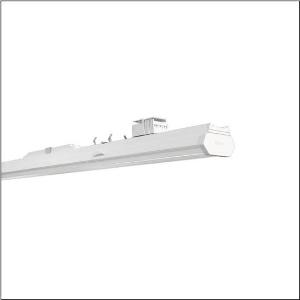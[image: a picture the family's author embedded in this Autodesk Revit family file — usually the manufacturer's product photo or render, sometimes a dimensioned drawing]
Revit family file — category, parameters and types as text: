
# Revit family: licross_r__11_protected_ho_51td13mn4gxs_7737
name_source: partatom
category: Lighting Fixtures
units: mm (PartAtom-declared; Revit-internal decimal feet)

## family parameters
Cut with Voids When Loaded = No
Host = Face
Light Source = No
Part Type = Normal
Room Calculation Point = No
Round Connector Dimension = Use Diameter
Shared = No

## types (1)
- --- (1 x LED, 16110 lm, 87.4 W, 4000K)
    Apparent Load = 87 VA
    CIE Flux Codes = 89 96 99 100 99
    Color Rendering = 80
    Color Temperature = 4000K
    Default Elevation = 1800 mm
    Description = Licross® 11 Protected HO, luminaire insert, of sheet steel, galvanised, coil coated, white, length: 1.500mm, width: 90mm, height: 101mm, LED rated luminous flux: 16.110lm, light colour: 840, control gear: ON/OFF Multilumen, with plug, 3-pole, with phase selection, mains connection: 220..240V, AC, 50/60Hz, rated input power: 87W, halogen-free wiring, primary light control with lens, of plastic, primary optical cover: cover, of PMMA, light emission: direct distribution, primary light characteristic: symmetric, protection rating (complete): IP54, insulation class (complete): insulation class I (protective earthing), certification: CE, ENEC, VDE, UKCA, protection symbol: D if used in an environment with non-conductive dust loads with corresponding accessories, impact resistance: IK06, permissible ambient temperature for indoor applications: -35..+35°C, corresponds to IFS (International Featured Standards) requirements for safety and quality in the food industry, reducing of maximum allowable ambient temperature of 5°C with ceiling mounting, LABS conformity tested according to VDMA 24364:2018-05, packaging unit: 1 piece
    Height = 92 mm
    Lamp = 1 x LED
    Lamp Light Flux = 16110 lm
    Lamp Power = 87.4 W
    Lamp count = 1
    Length = 1500 mm
    Luminous efficacy = 184 lm/W
    Manufacturer = Siteco
    ModVariant = No
    Model = 51TD13MN4GXS
    Mounting Place = Ceiling
    Mounting Type = Pendant
    Number of Poles = 1
    OnlyDefault = Yes
    Power Factor = 1
    Product Name = Licross® 11 Protected HO
    Product group = luminaire insert
    ProductGroupID = 901
    Protection Class = Protection class I
    Protection Degree = IP 54
    RLX_Detail_Level = 1
    RLX_Emergency_Light_Flux = 0 lm
    RLX_Emergency_Type = 0
    RLX_Emergency_Type_DB = No
    RlxData = <blob elided: 21925 chars, md5=d7e3c343>
    Socket = socket
    Standby Power = 0 W
    System Light Flux = 16110 lm
    System Power = 87 W
    Type Comments = factory setting: luminous flux: 100 % | (A | C | E) | 203 mA
    Type Image = l_1256145.jpg
    URL = http://relux.com
    VarID = @adj_055087
    Voltage = 0 V
    Weight = 0.00 kg
    Width = 88 mm

## geometry (parser evidence)
native form markers: Blend x4, Sweep x11
no freeform markers — native parametric forms only
